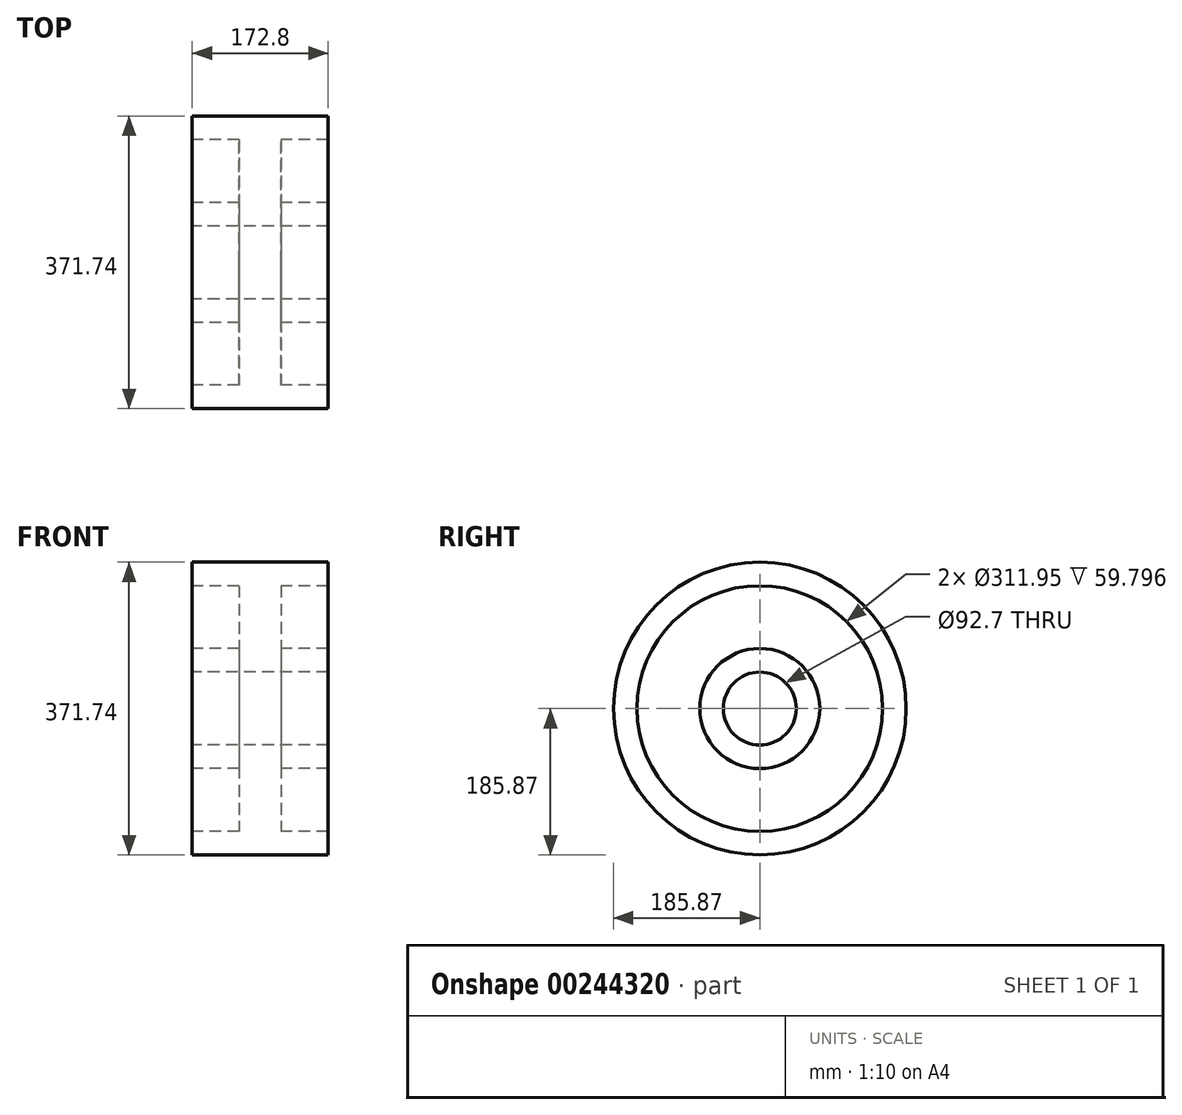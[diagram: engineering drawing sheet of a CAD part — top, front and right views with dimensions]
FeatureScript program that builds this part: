
annotation { "Feature Type Name" : "Feature", "Feature Type Description" : "" }
export const myFeature = defineFeature(function(context is Context, id is Id, definition is map)
    precondition{}
    {
        {
            var Q0;
            Q0=qCreatedBy(makeId("Front.planeOp"),FACE);
            var sketch = newSketch(context, id + "F0", { "sketchPlane" : qUnion([Q0])});
            skLineSegment(sketch, "E0", {"start": v(-121.3, 0) * mm, "end": v(123.84, 0) * mm, "construction": true});
            skLineSegment(sketch, "E1", {"start": v(-86.4, 46.35) * mm, "end": v(-86.4, 76.25) * mm});
            skLineSegment(sketch, "E2", {"start": v(-86.4, 76.25) * mm, "end": v(-26.6, 76.25) * mm});
            skLineSegment(sketch, "E3", {"start": v(-26.6, 76.25) * mm, "end": v(-26.6, 155.98) * mm});
            skLineSegment(sketch, "E4", {"start": v(-26.6, 155.98) * mm, "end": v(-86.4, 155.98) * mm});
            skLineSegment(sketch, "E5", {"start": v(-86.4, 155.98) * mm, "end": v(-86.4, 185.87) * mm});
            skLineSegment(sketch, "E6", {"start": v(-86.4, 185.87) * mm, "end": v(86.4, 185.87) * mm});
            skLineSegment(sketch, "E7", {"start": v(86.4, 185.87) * mm, "end": v(86.4, 155.98) * mm});
            skLineSegment(sketch, "E8", {"start": v(0, 203.67) * mm, "end": v(0, 0) * mm, "construction": true});
            skLineSegment(sketch, "E9", {"start": v(86.4, 155.98) * mm, "end": v(26.6, 155.98) * mm});
            skLineSegment(sketch, "E10", {"start": v(26.6, 155.98) * mm, "end": v(26.6, 76.25) * mm});
            skLineSegment(sketch, "E11", {"start": v(26.6, 76.25) * mm, "end": v(86.4, 76.25) * mm});
            skLineSegment(sketch, "E12", {"start": v(86.4, 76.25) * mm, "end": v(86.4, 46.35) * mm});
            skLineSegment(sketch, "E13", {"start": v(86.4, 46.35) * mm, "end": v(-86.4, 46.35) * mm});
            skSolve(sketch);
        }
        {
            var Q0;
            Q0=makeQuery(id+"F0.imprint","IMPRINT",FACE,{"disambiguationData":[TD([[makeQuery(id+"F0.imprint","IMPRINT",EDGE,{"derivedFrom":sQuery(id+"F0.wireOp",EDGE,"E1")}),-1.0]])]});
            var Q1;
            Q1=sQuery(id+"F0.wireOp",EDGE,"E0");
            revolve(context, id + "F1", {"entities" : qUnion([Q0]), "axis" : qUnion([Q1]), "revolveType" : RevolveType.FULL});
        }
    });
